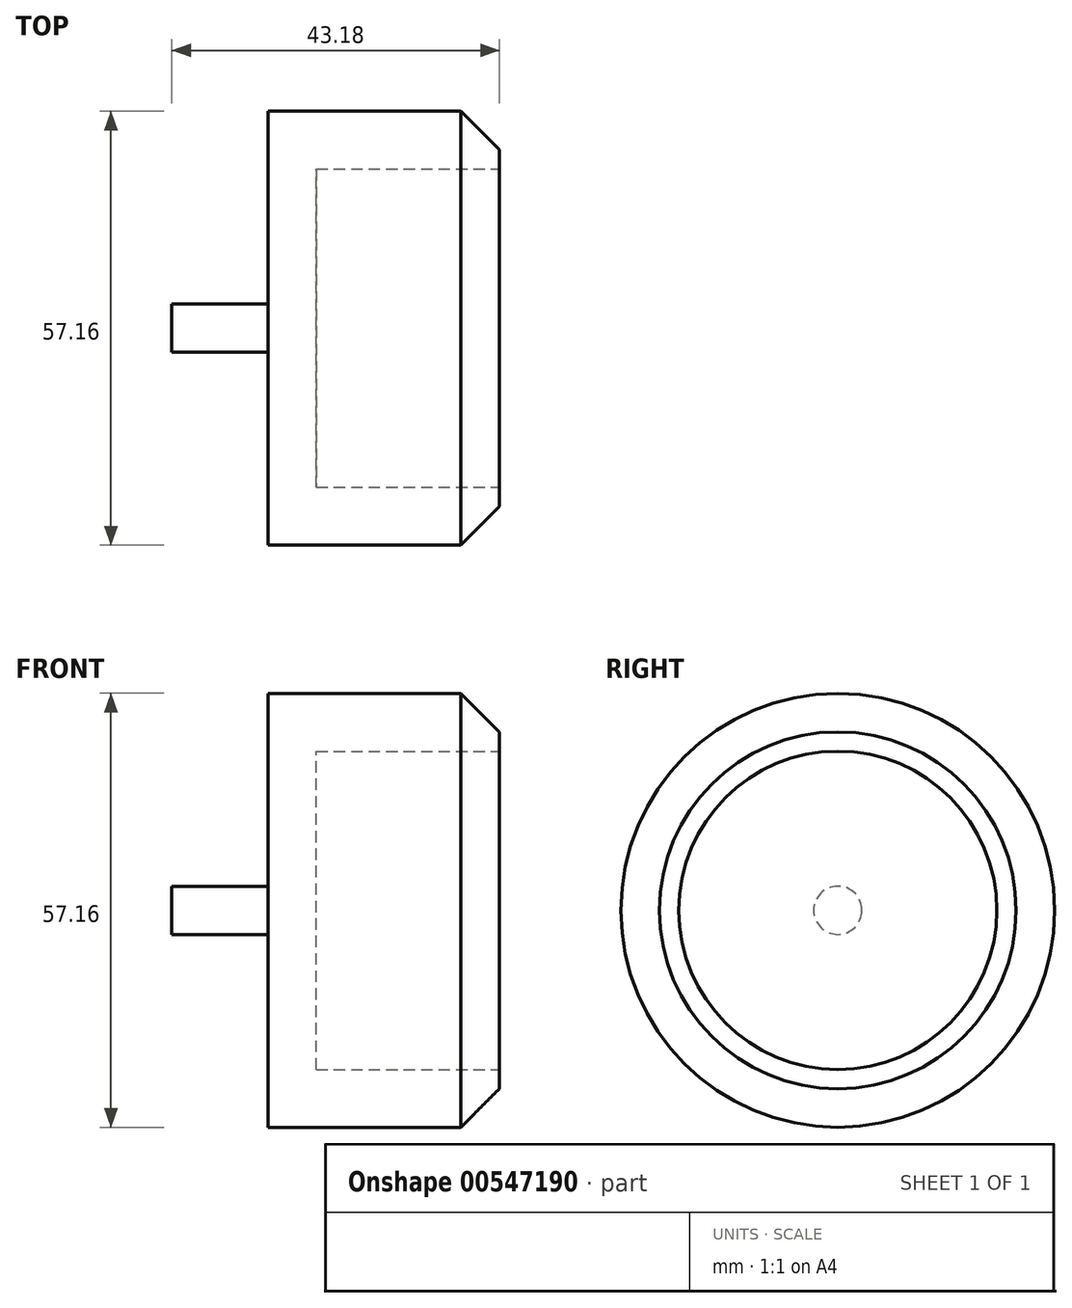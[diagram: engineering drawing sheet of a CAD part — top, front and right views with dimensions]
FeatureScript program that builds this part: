
annotation { "Feature Type Name" : "Feature", "Feature Type Description" : "" }
export const myFeature = defineFeature(function(context is Context, id is Id, definition is map)
    precondition{}
    {
        {
            var Q0;
            Q0=qCreatedBy(makeId("Front.planeOp"),FACE);
            var sketch = newSketch(context, id + "F0", { "sketchPlane" : qUnion([Q0])});
            skLineSegment(sketch, "E0", {"start": v(0, 0) * mm, "end": v(0, 3.18) * mm});
            skLineSegment(sketch, "E1", {"start": v(0, 3.18) * mm, "end": v(12.7, 3.18) * mm});
            skLineSegment(sketch, "E2", {"start": v(12.7, 3.18) * mm, "end": v(12.7, 28.58) * mm});
            skLineSegment(sketch, "E3", {"start": v(19.05, 0) * mm, "end": v(0, 0) * mm});
            skLineSegment(sketch, "E4", {"start": v(12.7, 28.58) * mm, "end": v(19.05, 28.58) * mm});
            skLineSegment(sketch, "E5", {"start": v(19.05, 20.96) * mm, "end": v(19.05, 0) * mm});
            skPoint(sketch, "E6.orphan", {"position": v(12.7, 15.88) * mm});
            skPoint(sketch, "E7.orphan", {"position": v(28.57, 0) * mm});
            skLineSegment(sketch, "E8", {"start": v(12.7, 28.58) * mm, "end": v(38.1, 28.58) * mm});
            skLineSegment(sketch, "E9", {"start": v(43.18, 23.5) * mm, "end": v(43.18, 20.96) * mm});
            skLineSegment(sketch, "E10", {"start": v(43.18, 20.96) * mm, "end": v(19.05, 20.96) * mm});
            skLineSegment(sketch, "E11", {"start": v(38.1, 28.58) * mm, "end": v(43.18, 23.5) * mm});
            skSolve(sketch);
        }
        {
            var Q0;
            Q0=makeQuery(id+"F0.imprint","IMPRINT",FACE,{"disambiguationData":[TD([[makeQuery(id+"F0.imprint","IMPRINT",EDGE,{"derivedFrom":sQuery(id+"F0.wireOp",EDGE,"E0")}),-1.0]])]});
            var Q1;
            Q1=sQuery(id+"F0.wireOp",EDGE,"E3");
            revolve(context, id + "F1", {"entities" : qUnion([Q0]), "axis" : qUnion([Q1]), "revolveType" : RevolveType.FULL});
        }
    });
